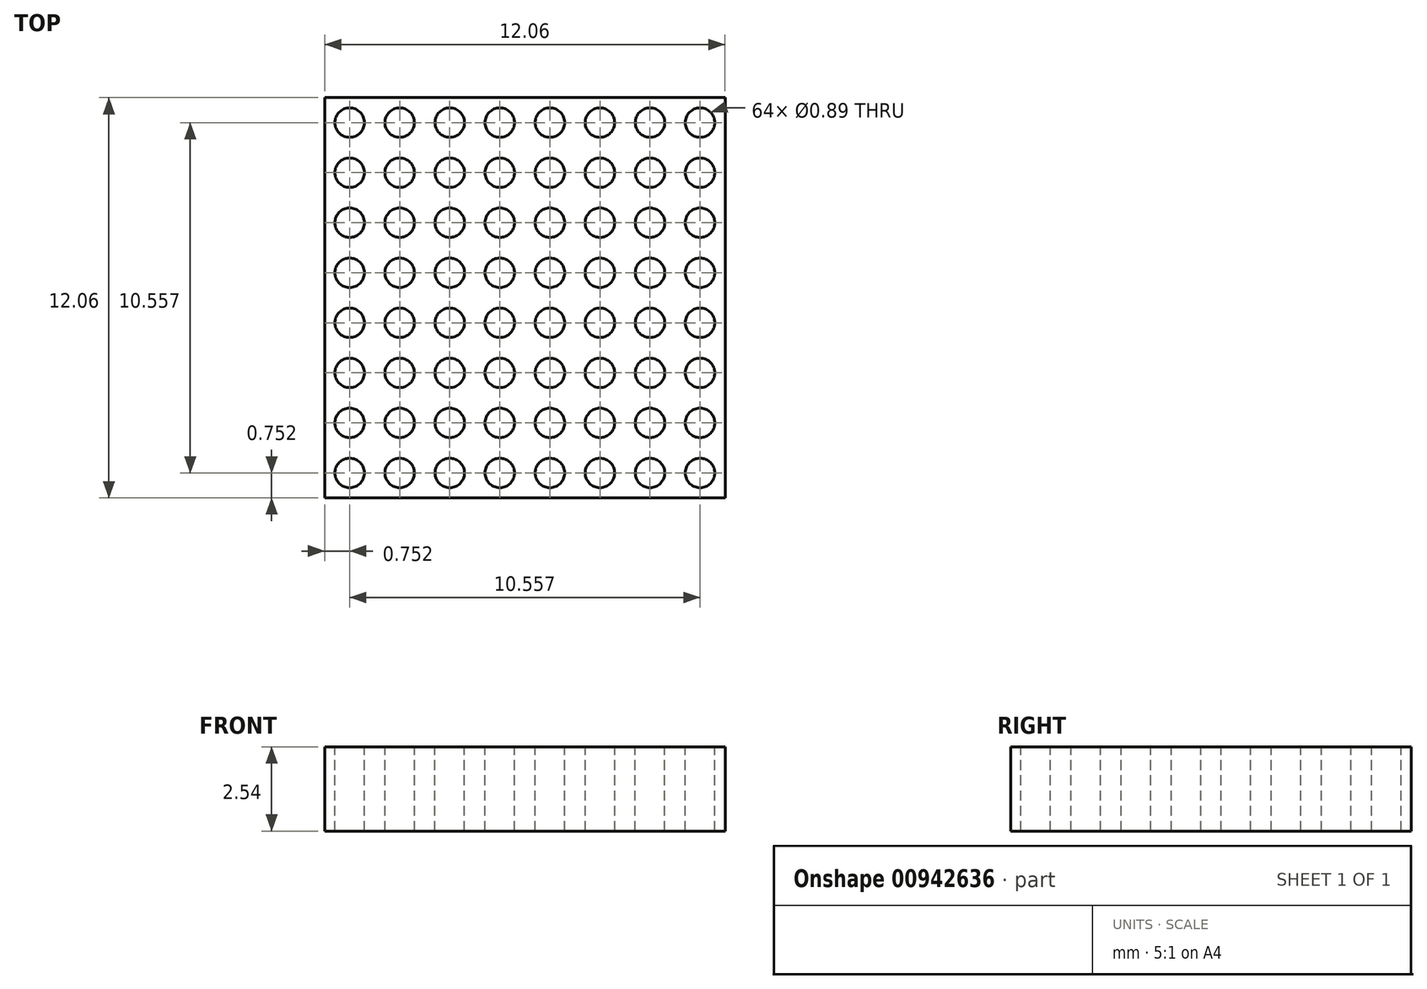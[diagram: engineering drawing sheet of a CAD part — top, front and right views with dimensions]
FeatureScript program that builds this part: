
annotation { "Feature Type Name" : "Feature", "Feature Type Description" : "" }
export const myFeature = defineFeature(function(context is Context, id is Id, definition is map)
    precondition{}
    {
        {
            var Q0;
            Q0=qCreatedBy(makeId("Top.planeOp"),FACE);
            var sketch = newSketch(context, id + "F0", { "sketchPlane" : qUnion([Q0])});
            skLineSegment(sketch, "E0.bottom", {"start": v(-6.03, 6.03) * mm, "end": v(6.03, 6.03) * mm});
            skLineSegment(sketch, "E0.top", {"start": v(-6.03, -6.03) * mm, "end": v(6.03, -6.03) * mm});
            skLineSegment(sketch, "E0.left", {"start": v(-6.03, 6.03) * mm, "end": v(-6.03, -6.03) * mm});
            skLineSegment(sketch, "E0.right", {"start": v(6.03, 6.03) * mm, "end": v(6.03, -6.03) * mm});
            skLineSegment(sketch, "E1", {"start": v(-6.03, 6.03) * mm, "end": v(6.03, -6.03) * mm, "construction": true});
            skSolve(sketch);
        }
        {
            var Q0;
            Q0=makeQuery(id+"F0.imprint","IMPRINT",FACE,{"disambiguationData":[TD([[makeQuery(id+"F0.imprint","IMPRINT",EDGE,{"derivedFrom":sQuery(id+"F0.wireOp",EDGE,"E0.bottom")}),-1.0]])]});
            extrude(context, id + "F1", {"entities" : qUnion([Q0]), "oppositeDirection" : true, "depth" : 2.54 * mm, "offsetDistance" : 25.4 * mm});
        }
        {
            var Q0;
            Q0=makeQuery(id+"F1.opExtrude","CAP_FACE",FACE,{"disambiguationData":[OSD([sQuery(id+"F0.wireOp",EDGE,"E0.bottom"),sQuery(id+"F0.wireOp",EDGE,"E0.top"),sQuery(id+"F0.wireOp",EDGE,"E0.left"),sQuery(id+"F0.wireOp",EDGE,"E0.right")])],"isStart":true});
            var sketch = newSketch(context, id + "F2", { "sketchPlane" : qUnion([Q0])});
            skCircle(sketch, "E2", {"center": v(-5.28, 5.28) * mm, "radius": 0.44 * mm});
            skCircle(sketch, "E3.1.0.0", {"center": v(-3.77, 5.28) * mm, "radius": 0.44 * mm});
            skCircle(sketch, "E3.2.0.0", {"center": v(-2.26, 5.28) * mm, "radius": 0.44 * mm});
            skCircle(sketch, "E3.3.0.0", {"center": v(-0.75, 5.28) * mm, "radius": 0.44 * mm});
            skCircle(sketch, "E3.4.0.0", {"center": v(0.75, 5.28) * mm, "radius": 0.44 * mm});
            skCircle(sketch, "E3.5.0.0", {"center": v(2.26, 5.28) * mm, "radius": 0.44 * mm});
            skCircle(sketch, "E3.6.0.0", {"center": v(3.77, 5.28) * mm, "radius": 0.44 * mm});
            skCircle(sketch, "E3.7.0.0", {"center": v(5.28, 5.28) * mm, "radius": 0.44 * mm});
            skLineSegment(sketch, "E3.direction1", {"start": v(-5.28, 5.28) * mm, "end": v(-3.77, 5.28) * mm, "construction": true});
            skPoint(sketch, "E4.0", {"position": v(-6.03, 6.03) * mm});
            skLineSegment(sketch, "E5.bottom", {"start": v(-6.03, 6.03) * mm, "end": v(-5.28, 6.03) * mm, "construction": true});
            skLineSegment(sketch, "E5.top", {"start": v(-6.03, 5.28) * mm, "end": v(-5.28, 5.28) * mm, "construction": true});
            skLineSegment(sketch, "E5.left", {"start": v(-6.03, 6.03) * mm, "end": v(-6.03, 5.28) * mm, "construction": true});
            skLineSegment(sketch, "E5.right", {"start": v(-5.28, 6.03) * mm, "end": v(-5.28, 5.28) * mm, "construction": true});
            skCircle(sketch, "E6.1.0.0", {"center": v(-5.28, 3.77) * mm, "radius": 0.44 * mm});
            skCircle(sketch, "E6.1.0.1", {"center": v(-3.77, 3.77) * mm, "radius": 0.44 * mm});
            skCircle(sketch, "E6.1.0.2", {"center": v(-2.26, 3.77) * mm, "radius": 0.44 * mm});
            skCircle(sketch, "E6.1.0.3", {"center": v(-0.75, 3.77) * mm, "radius": 0.44 * mm});
            skCircle(sketch, "E6.1.0.4", {"center": v(0.75, 3.77) * mm, "radius": 0.44 * mm});
            skCircle(sketch, "E6.1.0.5", {"center": v(2.26, 3.77) * mm, "radius": 0.44 * mm});
            skCircle(sketch, "E6.1.0.6", {"center": v(3.77, 3.77) * mm, "radius": 0.44 * mm});
            skCircle(sketch, "E6.1.0.7", {"center": v(5.28, 3.77) * mm, "radius": 0.44 * mm});
            skCircle(sketch, "E6.2.0.0", {"center": v(-5.28, 2.26) * mm, "radius": 0.44 * mm});
            skCircle(sketch, "E6.2.0.1", {"center": v(-3.77, 2.26) * mm, "radius": 0.44 * mm});
            skCircle(sketch, "E6.2.0.2", {"center": v(-2.26, 2.26) * mm, "radius": 0.44 * mm});
            skCircle(sketch, "E6.2.0.3", {"center": v(-0.75, 2.26) * mm, "radius": 0.44 * mm});
            skCircle(sketch, "E6.2.0.4", {"center": v(0.75, 2.26) * mm, "radius": 0.44 * mm});
            skCircle(sketch, "E6.2.0.5", {"center": v(2.26, 2.26) * mm, "radius": 0.44 * mm});
            skCircle(sketch, "E6.2.0.6", {"center": v(3.77, 2.26) * mm, "radius": 0.44 * mm});
            skCircle(sketch, "E6.2.0.7", {"center": v(5.28, 2.26) * mm, "radius": 0.44 * mm});
            skCircle(sketch, "E6.3.0.0", {"center": v(-5.28, 0.75) * mm, "radius": 0.44 * mm});
            skCircle(sketch, "E6.3.0.1", {"center": v(-3.77, 0.75) * mm, "radius": 0.44 * mm});
            skCircle(sketch, "E6.3.0.2", {"center": v(-2.26, 0.75) * mm, "radius": 0.44 * mm});
            skCircle(sketch, "E6.3.0.3", {"center": v(-0.75, 0.75) * mm, "radius": 0.44 * mm});
            skCircle(sketch, "E6.3.0.4", {"center": v(0.75, 0.75) * mm, "radius": 0.44 * mm});
            skCircle(sketch, "E6.3.0.5", {"center": v(2.26, 0.75) * mm, "radius": 0.44 * mm});
            skCircle(sketch, "E6.3.0.6", {"center": v(3.77, 0.75) * mm, "radius": 0.44 * mm});
            skCircle(sketch, "E6.3.0.7", {"center": v(5.28, 0.75) * mm, "radius": 0.44 * mm});
            skCircle(sketch, "E6.4.0.0", {"center": v(-5.28, -0.75) * mm, "radius": 0.44 * mm});
            skCircle(sketch, "E6.4.0.1", {"center": v(-3.77, -0.75) * mm, "radius": 0.44 * mm});
            skCircle(sketch, "E6.4.0.2", {"center": v(-2.26, -0.75) * mm, "radius": 0.44 * mm});
            skCircle(sketch, "E6.4.0.3", {"center": v(-0.75, -0.75) * mm, "radius": 0.44 * mm});
            skCircle(sketch, "E6.4.0.4", {"center": v(0.75, -0.75) * mm, "radius": 0.44 * mm});
            skCircle(sketch, "E6.4.0.5", {"center": v(2.26, -0.75) * mm, "radius": 0.44 * mm});
            skCircle(sketch, "E6.4.0.6", {"center": v(3.77, -0.75) * mm, "radius": 0.44 * mm});
            skCircle(sketch, "E6.4.0.7", {"center": v(5.28, -0.75) * mm, "radius": 0.44 * mm});
            skCircle(sketch, "E6.5.0.0", {"center": v(-5.28, -2.26) * mm, "radius": 0.44 * mm});
            skCircle(sketch, "E6.5.0.1", {"center": v(-3.77, -2.26) * mm, "radius": 0.44 * mm});
            skCircle(sketch, "E6.5.0.2", {"center": v(-2.26, -2.26) * mm, "radius": 0.44 * mm});
            skCircle(sketch, "E6.5.0.3", {"center": v(-0.75, -2.26) * mm, "radius": 0.44 * mm});
            skCircle(sketch, "E6.5.0.4", {"center": v(0.75, -2.26) * mm, "radius": 0.44 * mm});
            skCircle(sketch, "E6.5.0.5", {"center": v(2.26, -2.26) * mm, "radius": 0.44 * mm});
            skCircle(sketch, "E6.5.0.6", {"center": v(3.77, -2.26) * mm, "radius": 0.44 * mm});
            skCircle(sketch, "E6.5.0.7", {"center": v(5.28, -2.26) * mm, "radius": 0.44 * mm});
            skCircle(sketch, "E6.6.0.0", {"center": v(-5.28, -3.77) * mm, "radius": 0.44 * mm});
            skCircle(sketch, "E6.6.0.1", {"center": v(-3.77, -3.77) * mm, "radius": 0.44 * mm});
            skCircle(sketch, "E6.6.0.2", {"center": v(-2.26, -3.77) * mm, "radius": 0.44 * mm});
            skCircle(sketch, "E6.6.0.3", {"center": v(-0.75, -3.77) * mm, "radius": 0.44 * mm});
            skCircle(sketch, "E6.6.0.4", {"center": v(0.75, -3.77) * mm, "radius": 0.44 * mm});
            skCircle(sketch, "E6.6.0.5", {"center": v(2.26, -3.77) * mm, "radius": 0.44 * mm});
            skCircle(sketch, "E6.6.0.6", {"center": v(3.77, -3.77) * mm, "radius": 0.44 * mm});
            skCircle(sketch, "E6.6.0.7", {"center": v(5.28, -3.77) * mm, "radius": 0.44 * mm});
            skCircle(sketch, "E6.7.0.0", {"center": v(-5.28, -5.28) * mm, "radius": 0.44 * mm});
            skCircle(sketch, "E6.7.0.1", {"center": v(-3.77, -5.28) * mm, "radius": 0.44 * mm});
            skCircle(sketch, "E6.7.0.2", {"center": v(-2.26, -5.28) * mm, "radius": 0.44 * mm});
            skCircle(sketch, "E6.7.0.3", {"center": v(-0.75, -5.28) * mm, "radius": 0.44 * mm});
            skCircle(sketch, "E6.7.0.4", {"center": v(0.75, -5.28) * mm, "radius": 0.44 * mm});
            skCircle(sketch, "E6.7.0.5", {"center": v(2.26, -5.28) * mm, "radius": 0.44 * mm});
            skCircle(sketch, "E6.7.0.6", {"center": v(3.77, -5.28) * mm, "radius": 0.44 * mm});
            skCircle(sketch, "E6.7.0.7", {"center": v(5.28, -5.28) * mm, "radius": 0.44 * mm});
            skLineSegment(sketch, "E6.direction1", {"start": v(-5.28, 5.28) * mm, "end": v(-5.28, 3.77) * mm, "construction": true});
            skSolve(sketch);
        }
        {
            var Q0;
            Q0=makeQuery(id+"F2.imprint","IMPRINT",FACE,{"disambiguationData":[TD([[makeQuery(id+"F2.imprint","IMPRINT",EDGE,{"derivedFrom":sQuery(id+"F2.wireOp",EDGE,"E2")}),1.0]])]});
            var Q1;
            Q1=makeQuery(id+"F2.imprint","IMPRINT",FACE,{"disambiguationData":[TD([[makeQuery(id+"F2.imprint","IMPRINT",EDGE,{"derivedFrom":sQuery(id+"F2.wireOp",EDGE,"E3.1.0.0")}),1.0]])]});
            var Q2;
            Q2=makeQuery(id+"F2.imprint","IMPRINT",FACE,{"disambiguationData":[TD([[makeQuery(id+"F2.imprint","IMPRINT",EDGE,{"derivedFrom":sQuery(id+"F2.wireOp",EDGE,"E6.1.0.0")}),1.0]])]});
            var Q3;
            Q3=makeQuery(id+"F2.imprint","IMPRINT",FACE,{"disambiguationData":[TD([[makeQuery(id+"F2.imprint","IMPRINT",EDGE,{"derivedFrom":sQuery(id+"F2.wireOp",EDGE,"E6.1.0.1")}),1.0]])]});
            var Q4;
            Q4=makeQuery(id+"F2.imprint","IMPRINT",FACE,{"disambiguationData":[TD([[makeQuery(id+"F2.imprint","IMPRINT",EDGE,{"derivedFrom":sQuery(id+"F2.wireOp",EDGE,"E3.2.0.0")}),1.0]])]});
            var Q5;
            Q5=makeQuery(id+"F2.imprint","IMPRINT",FACE,{"disambiguationData":[TD([[makeQuery(id+"F2.imprint","IMPRINT",EDGE,{"derivedFrom":sQuery(id+"F2.wireOp",EDGE,"E6.1.0.2")}),1.0]])]});
            var Q6;
            Q6=makeQuery(id+"F2.imprint","IMPRINT",FACE,{"disambiguationData":[TD([[makeQuery(id+"F2.imprint","IMPRINT",EDGE,{"derivedFrom":sQuery(id+"F2.wireOp",EDGE,"E6.1.0.3")}),1.0]])]});
            var Q7;
            Q7=makeQuery(id+"F2.imprint","IMPRINT",FACE,{"disambiguationData":[TD([[makeQuery(id+"F2.imprint","IMPRINT",EDGE,{"derivedFrom":sQuery(id+"F2.wireOp",EDGE,"E3.3.0.0")}),1.0]])]});
            var Q8;
            Q8=makeQuery(id+"F2.imprint","IMPRINT",FACE,{"disambiguationData":[TD([[makeQuery(id+"F2.imprint","IMPRINT",EDGE,{"derivedFrom":sQuery(id+"F2.wireOp",EDGE,"E6.2.0.3")}),1.0]])]});
            var Q9;
            Q9=makeQuery(id+"F2.imprint","IMPRINT",FACE,{"disambiguationData":[TD([[makeQuery(id+"F2.imprint","IMPRINT",EDGE,{"derivedFrom":sQuery(id+"F2.wireOp",EDGE,"E6.2.0.2")}),1.0]])]});
            var Q10;
            Q10=makeQuery(id+"F2.imprint","IMPRINT",FACE,{"disambiguationData":[TD([[makeQuery(id+"F2.imprint","IMPRINT",EDGE,{"derivedFrom":sQuery(id+"F2.wireOp",EDGE,"E6.2.0.0")}),1.0]])]});
            var Q11;
            Q11=makeQuery(id+"F2.imprint","IMPRINT",FACE,{"disambiguationData":[TD([[makeQuery(id+"F2.imprint","IMPRINT",EDGE,{"derivedFrom":sQuery(id+"F2.wireOp",EDGE,"E6.2.0.1")}),1.0]])]});
            var Q12;
            Q12=makeQuery(id+"F2.imprint","IMPRINT",FACE,{"disambiguationData":[TD([[makeQuery(id+"F2.imprint","IMPRINT",EDGE,{"derivedFrom":sQuery(id+"F2.wireOp",EDGE,"E6.2.0.4")}),1.0]])]});
            var Q13;
            Q13=makeQuery(id+"F2.imprint","IMPRINT",FACE,{"disambiguationData":[TD([[makeQuery(id+"F2.imprint","IMPRINT",EDGE,{"derivedFrom":sQuery(id+"F2.wireOp",EDGE,"E6.1.0.4")}),1.0]])]});
            var Q14;
            Q14=makeQuery(id+"F2.imprint","IMPRINT",FACE,{"disambiguationData":[TD([[makeQuery(id+"F2.imprint","IMPRINT",EDGE,{"derivedFrom":sQuery(id+"F2.wireOp",EDGE,"E3.4.0.0")}),1.0]])]});
            var Q15;
            Q15=makeQuery(id+"F2.imprint","IMPRINT",FACE,{"disambiguationData":[TD([[makeQuery(id+"F2.imprint","IMPRINT",EDGE,{"derivedFrom":sQuery(id+"F2.wireOp",EDGE,"E3.5.0.0")}),1.0]])]});
            var Q16;
            Q16=makeQuery(id+"F2.imprint","IMPRINT",FACE,{"disambiguationData":[TD([[makeQuery(id+"F2.imprint","IMPRINT",EDGE,{"derivedFrom":sQuery(id+"F2.wireOp",EDGE,"E6.1.0.5")}),1.0]])]});
            var Q17;
            Q17=makeQuery(id+"F2.imprint","IMPRINT",FACE,{"disambiguationData":[TD([[makeQuery(id+"F2.imprint","IMPRINT",EDGE,{"derivedFrom":sQuery(id+"F2.wireOp",EDGE,"E6.2.0.5")}),1.0]])]});
            var Q18;
            Q18=makeQuery(id+"F2.imprint","IMPRINT",FACE,{"disambiguationData":[TD([[makeQuery(id+"F2.imprint","IMPRINT",EDGE,{"derivedFrom":sQuery(id+"F2.wireOp",EDGE,"E6.7.0.0")}),1.0]])]});
            var Q19;
            Q19=makeQuery(id+"F2.imprint","IMPRINT",FACE,{"disambiguationData":[TD([[makeQuery(id+"F2.imprint","IMPRINT",EDGE,{"derivedFrom":sQuery(id+"F2.wireOp",EDGE,"E6.6.0.0")}),1.0]])]});
            var Q20;
            Q20=makeQuery(id+"F2.imprint","IMPRINT",FACE,{"disambiguationData":[TD([[makeQuery(id+"F2.imprint","IMPRINT",EDGE,{"derivedFrom":sQuery(id+"F2.wireOp",EDGE,"E6.5.0.0")}),1.0]])]});
            var Q21;
            Q21=makeQuery(id+"F2.imprint","IMPRINT",FACE,{"disambiguationData":[TD([[makeQuery(id+"F2.imprint","IMPRINT",EDGE,{"derivedFrom":sQuery(id+"F2.wireOp",EDGE,"E6.4.0.0")}),1.0]])]});
            var Q22;
            Q22=makeQuery(id+"F2.imprint","IMPRINT",FACE,{"disambiguationData":[TD([[makeQuery(id+"F2.imprint","IMPRINT",EDGE,{"derivedFrom":sQuery(id+"F2.wireOp",EDGE,"E6.3.0.0")}),1.0]])]});
            var Q23;
            Q23=makeQuery(id+"F2.imprint","IMPRINT",FACE,{"disambiguationData":[TD([[makeQuery(id+"F2.imprint","IMPRINT",EDGE,{"derivedFrom":sQuery(id+"F2.wireOp",EDGE,"E6.3.0.1")}),1.0]])]});
            var Q24;
            Q24=makeQuery(id+"F2.imprint","IMPRINT",FACE,{"disambiguationData":[TD([[makeQuery(id+"F2.imprint","IMPRINT",EDGE,{"derivedFrom":sQuery(id+"F2.wireOp",EDGE,"E6.4.0.1")}),1.0]])]});
            var Q25;
            Q25=makeQuery(id+"F2.imprint","IMPRINT",FACE,{"disambiguationData":[TD([[makeQuery(id+"F2.imprint","IMPRINT",EDGE,{"derivedFrom":sQuery(id+"F2.wireOp",EDGE,"E6.5.0.1")}),1.0]])]});
            var Q26;
            Q26=makeQuery(id+"F2.imprint","IMPRINT",FACE,{"disambiguationData":[TD([[makeQuery(id+"F2.imprint","IMPRINT",EDGE,{"derivedFrom":sQuery(id+"F2.wireOp",EDGE,"E6.6.0.1")}),1.0]])]});
            var Q27;
            Q27=makeQuery(id+"F2.imprint","IMPRINT",FACE,{"disambiguationData":[TD([[makeQuery(id+"F2.imprint","IMPRINT",EDGE,{"derivedFrom":sQuery(id+"F2.wireOp",EDGE,"E6.7.0.1")}),1.0]])]});
            var Q28;
            Q28=makeQuery(id+"F2.imprint","IMPRINT",FACE,{"disambiguationData":[TD([[makeQuery(id+"F2.imprint","IMPRINT",EDGE,{"derivedFrom":sQuery(id+"F2.wireOp",EDGE,"E6.7.0.2")}),1.0]])]});
            var Q29;
            Q29=makeQuery(id+"F2.imprint","IMPRINT",FACE,{"disambiguationData":[TD([[makeQuery(id+"F2.imprint","IMPRINT",EDGE,{"derivedFrom":sQuery(id+"F2.wireOp",EDGE,"E6.6.0.2")}),1.0]])]});
            var Q30;
            Q30=makeQuery(id+"F2.imprint","IMPRINT",FACE,{"disambiguationData":[TD([[makeQuery(id+"F2.imprint","IMPRINT",EDGE,{"derivedFrom":sQuery(id+"F2.wireOp",EDGE,"E6.5.0.2")}),1.0]])]});
            var Q31;
            Q31=makeQuery(id+"F2.imprint","IMPRINT",FACE,{"disambiguationData":[TD([[makeQuery(id+"F2.imprint","IMPRINT",EDGE,{"derivedFrom":sQuery(id+"F2.wireOp",EDGE,"E6.4.0.2")}),1.0]])]});
            var Q32;
            Q32=makeQuery(id+"F2.imprint","IMPRINT",FACE,{"disambiguationData":[TD([[makeQuery(id+"F2.imprint","IMPRINT",EDGE,{"derivedFrom":sQuery(id+"F2.wireOp",EDGE,"E6.3.0.2")}),1.0]])]});
            var Q33;
            Q33=makeQuery(id+"F2.imprint","IMPRINT",FACE,{"disambiguationData":[TD([[makeQuery(id+"F2.imprint","IMPRINT",EDGE,{"derivedFrom":sQuery(id+"F2.wireOp",EDGE,"E6.3.0.3")}),1.0]])]});
            var Q34;
            Q34=makeQuery(id+"F2.imprint","IMPRINT",FACE,{"disambiguationData":[TD([[makeQuery(id+"F2.imprint","IMPRINT",EDGE,{"derivedFrom":sQuery(id+"F2.wireOp",EDGE,"E6.3.0.4")}),1.0]])]});
            var Q35;
            Q35=makeQuery(id+"F2.imprint","IMPRINT",FACE,{"disambiguationData":[TD([[makeQuery(id+"F2.imprint","IMPRINT",EDGE,{"derivedFrom":sQuery(id+"F2.wireOp",EDGE,"E6.3.0.5")}),1.0]])]});
            var Q36;
            Q36=makeQuery(id+"F2.imprint","IMPRINT",FACE,{"disambiguationData":[TD([[makeQuery(id+"F2.imprint","IMPRINT",EDGE,{"derivedFrom":sQuery(id+"F2.wireOp",EDGE,"E6.4.0.5")}),1.0]])]});
            var Q37;
            Q37=makeQuery(id+"F2.imprint","IMPRINT",FACE,{"disambiguationData":[TD([[makeQuery(id+"F2.imprint","IMPRINT",EDGE,{"derivedFrom":sQuery(id+"F2.wireOp",EDGE,"E6.4.0.4")}),1.0]])]});
            var Q38;
            Q38=makeQuery(id+"F2.imprint","IMPRINT",FACE,{"disambiguationData":[TD([[makeQuery(id+"F2.imprint","IMPRINT",EDGE,{"derivedFrom":sQuery(id+"F2.wireOp",EDGE,"E6.4.0.3")}),1.0]])]});
            var Q39;
            Q39=makeQuery(id+"F2.imprint","IMPRINT",FACE,{"disambiguationData":[TD([[makeQuery(id+"F2.imprint","IMPRINT",EDGE,{"derivedFrom":sQuery(id+"F2.wireOp",EDGE,"E6.5.0.3")}),1.0]])]});
            var Q40;
            Q40=makeQuery(id+"F2.imprint","IMPRINT",FACE,{"disambiguationData":[TD([[makeQuery(id+"F2.imprint","IMPRINT",EDGE,{"derivedFrom":sQuery(id+"F2.wireOp",EDGE,"E6.5.0.4")}),1.0]])]});
            var Q41;
            Q41=makeQuery(id+"F2.imprint","IMPRINT",FACE,{"disambiguationData":[TD([[makeQuery(id+"F2.imprint","IMPRINT",EDGE,{"derivedFrom":sQuery(id+"F2.wireOp",EDGE,"E6.5.0.5")}),1.0]])]});
            var Q42;
            Q42=makeQuery(id+"F2.imprint","IMPRINT",FACE,{"disambiguationData":[TD([[makeQuery(id+"F2.imprint","IMPRINT",EDGE,{"derivedFrom":sQuery(id+"F2.wireOp",EDGE,"E6.6.0.5")}),1.0]])]});
            var Q43;
            Q43=makeQuery(id+"F2.imprint","IMPRINT",FACE,{"disambiguationData":[TD([[makeQuery(id+"F2.imprint","IMPRINT",EDGE,{"derivedFrom":sQuery(id+"F2.wireOp",EDGE,"E6.6.0.4")}),1.0]])]});
            var Q44;
            Q44=makeQuery(id+"F2.imprint","IMPRINT",FACE,{"disambiguationData":[TD([[makeQuery(id+"F2.imprint","IMPRINT",EDGE,{"derivedFrom":sQuery(id+"F2.wireOp",EDGE,"E6.6.0.3")}),1.0]])]});
            var Q45;
            Q45=makeQuery(id+"F2.imprint","IMPRINT",FACE,{"disambiguationData":[TD([[makeQuery(id+"F2.imprint","IMPRINT",EDGE,{"derivedFrom":sQuery(id+"F2.wireOp",EDGE,"E6.7.0.3")}),1.0]])]});
            var Q46;
            Q46=makeQuery(id+"F2.imprint","IMPRINT",FACE,{"disambiguationData":[TD([[makeQuery(id+"F2.imprint","IMPRINT",EDGE,{"derivedFrom":sQuery(id+"F2.wireOp",EDGE,"E6.7.0.4")}),1.0]])]});
            var Q47;
            Q47=makeQuery(id+"F2.imprint","IMPRINT",FACE,{"disambiguationData":[TD([[makeQuery(id+"F2.imprint","IMPRINT",EDGE,{"derivedFrom":sQuery(id+"F2.wireOp",EDGE,"E6.7.0.5")}),1.0]])]});
            var Q48;
            Q48=makeQuery(id+"F2.imprint","IMPRINT",FACE,{"disambiguationData":[TD([[makeQuery(id+"F2.imprint","IMPRINT",EDGE,{"derivedFrom":sQuery(id+"F2.wireOp",EDGE,"E6.6.0.7")}),1.0]])]});
            var Q49;
            Q49=makeQuery(id+"F2.imprint","IMPRINT",FACE,{"disambiguationData":[TD([[makeQuery(id+"F2.imprint","IMPRINT",EDGE,{"derivedFrom":sQuery(id+"F2.wireOp",EDGE,"E6.7.0.7")}),1.0]])]});
            var Q50;
            Q50=makeQuery(id+"F2.imprint","IMPRINT",FACE,{"disambiguationData":[TD([[makeQuery(id+"F2.imprint","IMPRINT",EDGE,{"derivedFrom":sQuery(id+"F2.wireOp",EDGE,"E6.5.0.7")}),1.0]])]});
            var Q51;
            Q51=makeQuery(id+"F2.imprint","IMPRINT",FACE,{"disambiguationData":[TD([[makeQuery(id+"F2.imprint","IMPRINT",EDGE,{"derivedFrom":sQuery(id+"F2.wireOp",EDGE,"E6.5.0.6")}),1.0]])]});
            var Q52;
            Q52=makeQuery(id+"F2.imprint","IMPRINT",FACE,{"disambiguationData":[TD([[makeQuery(id+"F2.imprint","IMPRINT",EDGE,{"derivedFrom":sQuery(id+"F2.wireOp",EDGE,"E6.4.0.6")}),1.0]])]});
            var Q53;
            Q53=makeQuery(id+"F2.imprint","IMPRINT",FACE,{"disambiguationData":[TD([[makeQuery(id+"F2.imprint","IMPRINT",EDGE,{"derivedFrom":sQuery(id+"F2.wireOp",EDGE,"E6.4.0.7")}),1.0]])]});
            var Q54;
            Q54=makeQuery(id+"F2.imprint","IMPRINT",FACE,{"disambiguationData":[TD([[makeQuery(id+"F2.imprint","IMPRINT",EDGE,{"derivedFrom":sQuery(id+"F2.wireOp",EDGE,"E6.3.0.7")}),1.0]])]});
            var Q55;
            Q55=makeQuery(id+"F2.imprint","IMPRINT",FACE,{"disambiguationData":[TD([[makeQuery(id+"F2.imprint","IMPRINT",EDGE,{"derivedFrom":sQuery(id+"F2.wireOp",EDGE,"E6.3.0.6")}),1.0]])]});
            var Q56;
            Q56=makeQuery(id+"F2.imprint","IMPRINT",FACE,{"disambiguationData":[TD([[makeQuery(id+"F2.imprint","IMPRINT",EDGE,{"derivedFrom":sQuery(id+"F2.wireOp",EDGE,"E6.2.0.6")}),1.0]])]});
            var Q57;
            Q57=makeQuery(id+"F2.imprint","IMPRINT",FACE,{"disambiguationData":[TD([[makeQuery(id+"F2.imprint","IMPRINT",EDGE,{"derivedFrom":sQuery(id+"F2.wireOp",EDGE,"E6.2.0.7")}),1.0]])]});
            var Q58;
            Q58=makeQuery(id+"F2.imprint","IMPRINT",FACE,{"disambiguationData":[TD([[makeQuery(id+"F2.imprint","IMPRINT",EDGE,{"derivedFrom":sQuery(id+"F2.wireOp",EDGE,"E6.1.0.6")}),1.0]])]});
            var Q59;
            Q59=makeQuery(id+"F2.imprint","IMPRINT",FACE,{"disambiguationData":[TD([[makeQuery(id+"F2.imprint","IMPRINT",EDGE,{"derivedFrom":sQuery(id+"F2.wireOp",EDGE,"E3.7.0.0")}),1.0]])]});
            var Q60;
            Q60=makeQuery(id+"F2.imprint","IMPRINT",FACE,{"disambiguationData":[TD([[makeQuery(id+"F2.imprint","IMPRINT",EDGE,{"derivedFrom":sQuery(id+"F2.wireOp",EDGE,"E6.1.0.7")}),1.0]])]});
            var Q61;
            Q61=makeQuery(id+"F2.imprint","IMPRINT",FACE,{"disambiguationData":[TD([[makeQuery(id+"F2.imprint","IMPRINT",EDGE,{"derivedFrom":sQuery(id+"F2.wireOp",EDGE,"E3.6.0.0")}),1.0]])]});
            var Q62;
            Q62=makeQuery(id+"F2.imprint","IMPRINT",FACE,{"disambiguationData":[TD([[makeQuery(id+"F2.imprint","IMPRINT",EDGE,{"derivedFrom":sQuery(id+"F2.wireOp",EDGE,"E6.6.0.6")}),1.0]])]});
            var Q63;
            Q63=makeQuery(id+"F2.imprint","IMPRINT",FACE,{"disambiguationData":[TD([[makeQuery(id+"F2.imprint","IMPRINT",EDGE,{"derivedFrom":sQuery(id+"F2.wireOp",EDGE,"E6.7.0.6")}),1.0]])]});
            extrude(context, id + "F3", {"entities" : qUnion([Q0, Q1, Q2, Q3, Q4, Q5, Q6, Q7, Q8, Q9, Q10, Q11, Q12, Q13, Q14, Q15, Q16, Q17, Q18, Q19, Q20, Q21, Q22, Q23, Q24, Q25, Q26, Q27, Q28, Q29, Q30, Q31, Q32, Q33, Q34, Q35, Q36, Q37, Q38, Q39, Q40, Q41, Q42, Q43, Q44, Q45, Q46, Q47, Q48, Q49, Q50, Q51, Q52, Q53, Q54, Q55, Q56, Q57, Q58, Q59, Q60, Q61, Q62, Q63]), "operationType" : NewBodyOperationType.REMOVE, "endBound" : BoundingType.UP_TO_NEXT, "oppositeDirection" : true, "depth" : 25.4 * mm, "offsetDistance" : 25.4 * mm});
        }
    });
